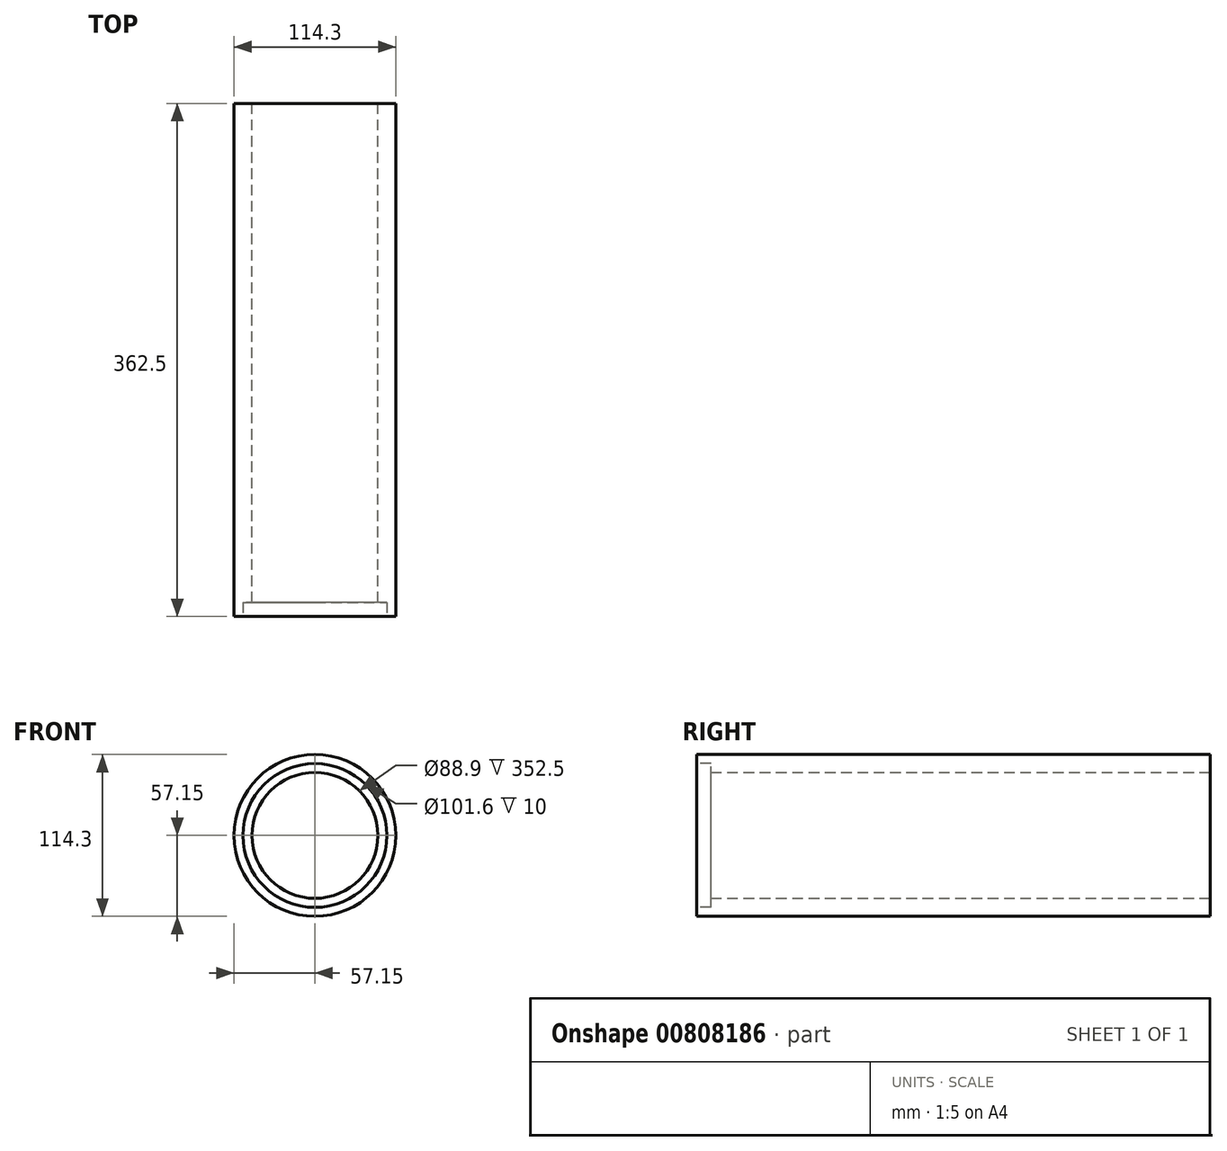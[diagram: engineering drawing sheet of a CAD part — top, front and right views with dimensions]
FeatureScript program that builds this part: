
annotation { "Feature Type Name" : "Feature", "Feature Type Description" : "" }
export const myFeature = defineFeature(function(context is Context, id is Id, definition is map)
    precondition{}
    {
        {
            var Q0;
            Q0=qCreatedBy(makeId("Front.planeOp"),FACE);
            var sketch = newSketch(context, id + "F0", { "sketchPlane" : qUnion([Q0])});
            skCircle(sketch, "E0", {"center": v(0, 0) * mm, "radius": 57.15 * mm});
            skCircle(sketch, "E1", {"center": v(0, 0) * mm, "radius": 44.45 * mm});
            skSolve(sketch);
        }
        {
            var Q0;
            Q0 = qSketchRegion(id + "F0", true);
            extrude(context, id + "F1", {"entities" : qUnion([Q0]), "depth" : 362.5 * mm, "offsetDistance" : 25 * mm});
        }
        {
            var Q0;
            Q0=makeQuery(id+"F1.opExtrude","CAP_FACE",FACE,{"disambiguationData":[OSD([sQuery(id+"F0.wireOp",EDGE,"E0"),sQuery(id+"F0.wireOp",EDGE,"E1")])],"isStart":false});
            var sketch = newSketch(context, id + "F2", { "sketchPlane" : qUnion([Q0])});
            skCircle(sketch, "E2", {"center": v(0, 0) * mm, "radius": 50.8 * mm});
            skCircle(sketch, "E3.0", {"center": v(0, 0) * mm, "radius": 44.45 * mm});
            skSolve(sketch);
        }
        {
            var Q0;
            Q0 = qSketchRegion(id + "F2", true);
            extrude(context, id + "F3", {"entities" : qUnion([Q0]), "operationType" : NewBodyOperationType.REMOVE, "oppositeDirection" : true, "depth" : 10 * mm, "offsetDistance" : 25 * mm});
        }
    });
